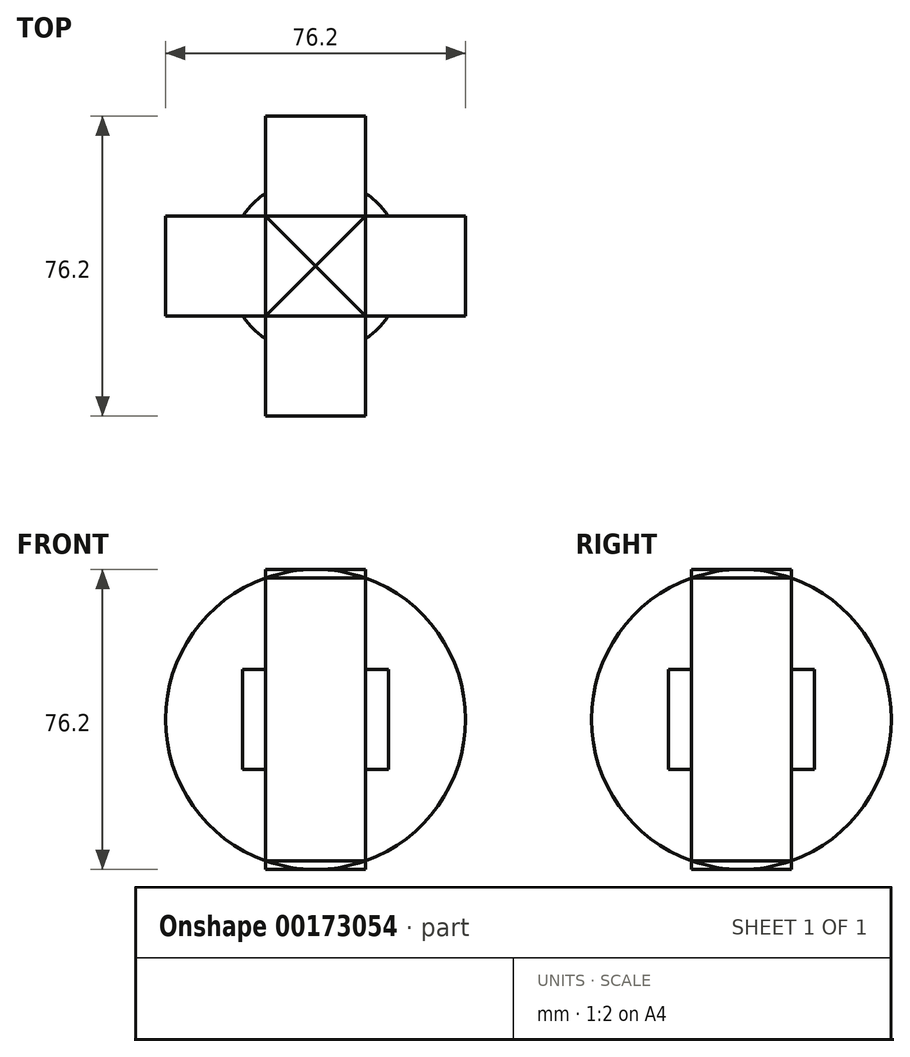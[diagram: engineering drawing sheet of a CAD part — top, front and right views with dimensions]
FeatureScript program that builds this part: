
annotation { "Feature Type Name" : "Feature", "Feature Type Description" : "" }
export const myFeature = defineFeature(function(context is Context, id is Id, definition is map)
    precondition{}
    {
        {
            var Q0;
            Q0=qCreatedBy(makeId("Top.planeOp"),FACE);
            var sketch = newSketch(context, id + "F0", { "sketchPlane" : qUnion([Q0])});
            skCircle(sketch, "E0", {"center": v(0, 0) * mm, "radius": 22.45 * mm});
            skSolve(sketch);
        }
        {
            var Q0;
            Q0=qCreatedBy(makeId("Front.planeOp"),FACE);
            var sketch = newSketch(context, id + "F1", { "sketchPlane" : qUnion([Q0])});
            skCircle(sketch, "E1", {"center": v(0, 0) * mm, "radius": 38.1 * mm});
            skSolve(sketch);
        }
        {
            var Q0;
            Q0=qCreatedBy(makeId("Right.planeOp"),FACE);
            var sketch = newSketch(context, id + "F2", { "sketchPlane" : qUnion([Q0])});
            skCircle(sketch, "E2", {"center": v(0, 0) * mm, "radius": 38.1 * mm});
            skSolve(sketch);
        }
        {
            var Q0;
            Q0=makeQuery(id+"F2.imprint","IMPRINT",FACE,{"disambiguationData":[TD([[makeQuery(id+"F2.imprint","IMPRINT",EDGE,{"derivedFrom":sQuery(id+"F2.wireOp",EDGE,"E2")}),1.0]])]});
            extrude(context, id + "F3", {"entities" : qUnion([Q0]), "endBound" : BoundingType.SYMMETRIC, "depth" : 25.4 * mm});
        }
        {
            var Q0;
            Q0=makeQuery(id+"F1.imprint","IMPRINT",FACE,{"disambiguationData":[TD([[makeQuery(id+"F1.imprint","IMPRINT",EDGE,{"derivedFrom":sQuery(id+"F1.wireOp",EDGE,"E1")}),1.0]])]});
            extrude(context, id + "F4", {"entities" : qUnion([Q0]), "operationType" : NewBodyOperationType.ADD, "endBound" : BoundingType.SYMMETRIC, "depth" : 25.4 * mm});
        }
        {
            var Q0;
            Q0=makeQuery(id+"F0.imprint","IMPRINT",FACE,{"disambiguationData":[TD([[makeQuery(id+"F0.imprint","IMPRINT",EDGE,{"derivedFrom":sQuery(id+"F0.wireOp",EDGE,"E0")}),1.0]])]});
            extrude(context, id + "F5", {"entities" : qUnion([Q0]), "operationType" : NewBodyOperationType.ADD, "endBound" : BoundingType.SYMMETRIC, "depth" : 25.4 * mm});
        }
    });
